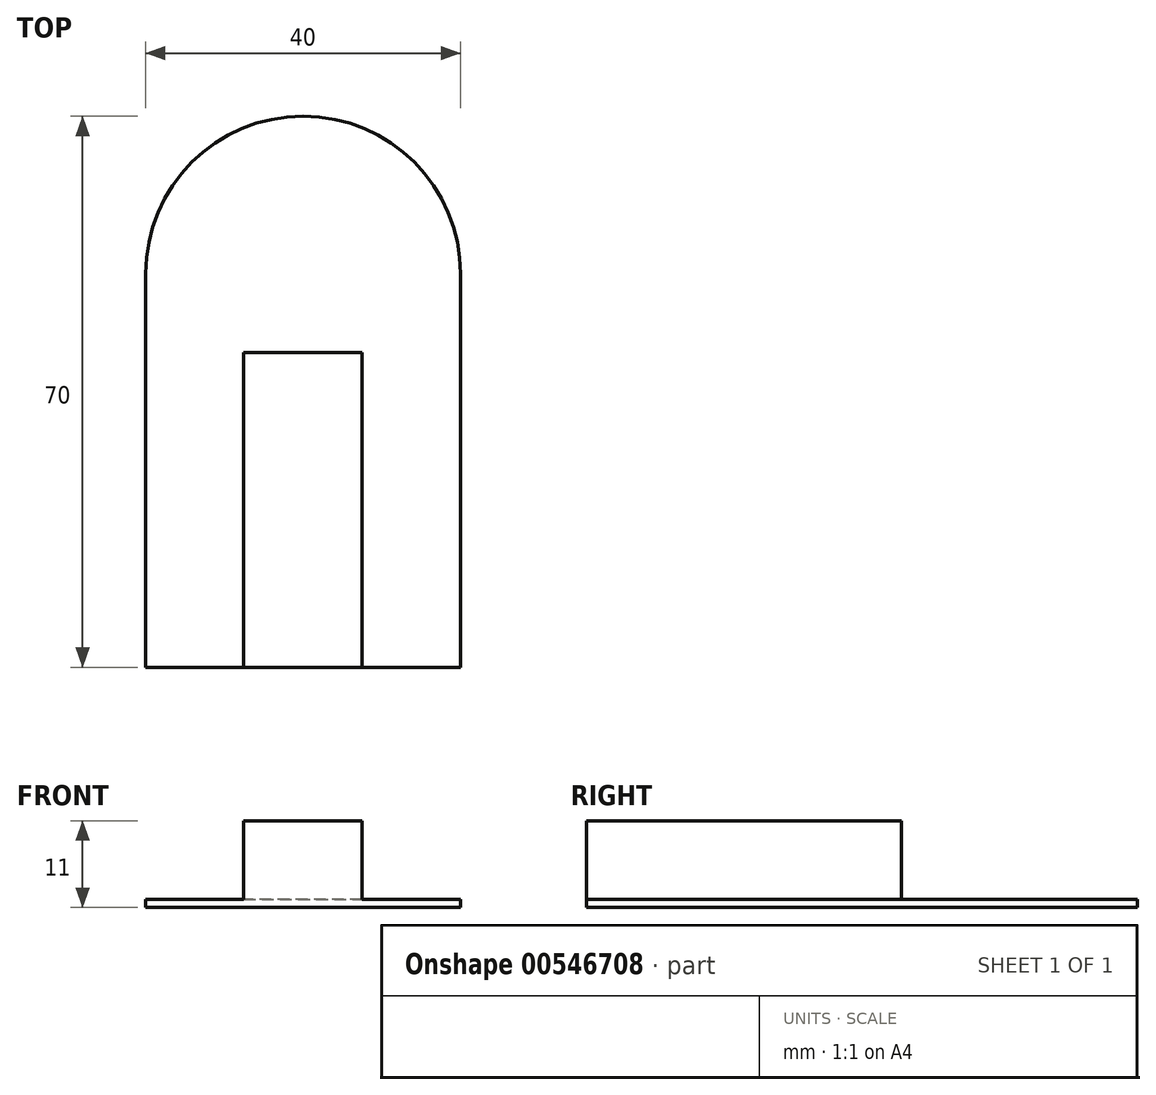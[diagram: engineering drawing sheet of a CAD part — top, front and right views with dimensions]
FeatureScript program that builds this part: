
annotation { "Feature Type Name" : "Feature", "Feature Type Description" : "" }
export const myFeature = defineFeature(function(context is Context, id is Id, definition is map)
    precondition{}
    {
        {
            var Q0;
            Q0=qCreatedBy(makeId("Top.planeOp"),FACE);
            var sketch = newSketch(context, id + "F0", { "sketchPlane" : qUnion([Q0])});
            skLineSegment(sketch, "E0.bottom", {"start": v(-134.65, 40.58) * mm, "end": v(-94.65, 40.58) * mm});
            skLineSegment(sketch, "E0.top", {"start": v(-134.65, -9.42) * mm, "end": v(-94.65, -9.42) * mm});
            skLineSegment(sketch, "E0.left", {"start": v(-134.65, 40.58) * mm, "end": v(-134.65, -9.42) * mm});
            skLineSegment(sketch, "E0.right", {"start": v(-94.65, 40.58) * mm, "end": v(-94.65, -9.42) * mm});
            skArc(sketch, "E1", {"start": v(-94.65, 40.58) * mm, "mid": v(-114.65, 60.58) * mm, "end": v(-134.65, 40.58) * mm});
            skSolve(sketch);
        }
        {
            var Q0;
            Q0=makeQuery(id+"F0.imprint","IMPRINT",FACE,{"disambiguationData":[TD([[makeQuery(id+"F0.imprint","IMPRINT",EDGE,{"derivedFrom":sQuery(id+"F0.wireOp",EDGE,"E0.bottom")}),-1.0]])]});
            var Q1;
            Q1=makeQuery(id+"F0.imprint","IMPRINT",FACE,{"disambiguationData":[TD([[makeQuery(id+"F0.imprint","IMPRINT",EDGE,{"derivedFrom":sQuery(id+"F0.wireOp",EDGE,"E0.bottom")}),1.0]])]});
            extrude(context, id + "F1", {"entities" : qUnion([Q0, Q1]), "depth" : 1 * mm, "offsetDistance" : 25.4 * mm});
        }
        {
            var Q0;
            Q0=makeQuery(id+"F1.opExtrude","CAP_FACE",FACE,{"disambiguationData":[OSD([sQuery(id+"F0.wireOp",EDGE,"E0.top"),sQuery(id+"F0.wireOp",EDGE,"E0.left"),sQuery(id+"F0.wireOp",EDGE,"E0.right"),sQuery(id+"F0.wireOp",EDGE,"E1")])],"isStart":false});
            var sketch = newSketch(context, id + "F2", { "sketchPlane" : qUnion([Q0])});
            skLineSegment(sketch, "E2.bottom", {"start": v(-122.18, -9.42) * mm, "end": v(-107.18, -9.42) * mm});
            skLineSegment(sketch, "E2.top", {"start": v(-122.18, 30.58) * mm, "end": v(-107.18, 30.58) * mm});
            skLineSegment(sketch, "E2.left", {"start": v(-122.18, -9.42) * mm, "end": v(-122.18, 30.58) * mm});
            skLineSegment(sketch, "E2.right", {"start": v(-107.18, -9.42) * mm, "end": v(-107.18, 30.58) * mm});
            skSolve(sketch);
        }
        {
            var Q0;
            Q0=makeQuery(id+"F2.imprint","IMPRINT",FACE,{"disambiguationData":[TD([[makeQuery(id+"F2.imprint","IMPRINT",EDGE,{"derivedFrom":sQuery(id+"F2.wireOp",EDGE,"E2.bottom")}),1.0]])]});
            extrude(context, id + "F3", {"entities" : qUnion([Q0]), "operationType" : NewBodyOperationType.ADD, "depth" : 10 * mm, "offsetDistance" : 25.4 * mm});
        }
    });
